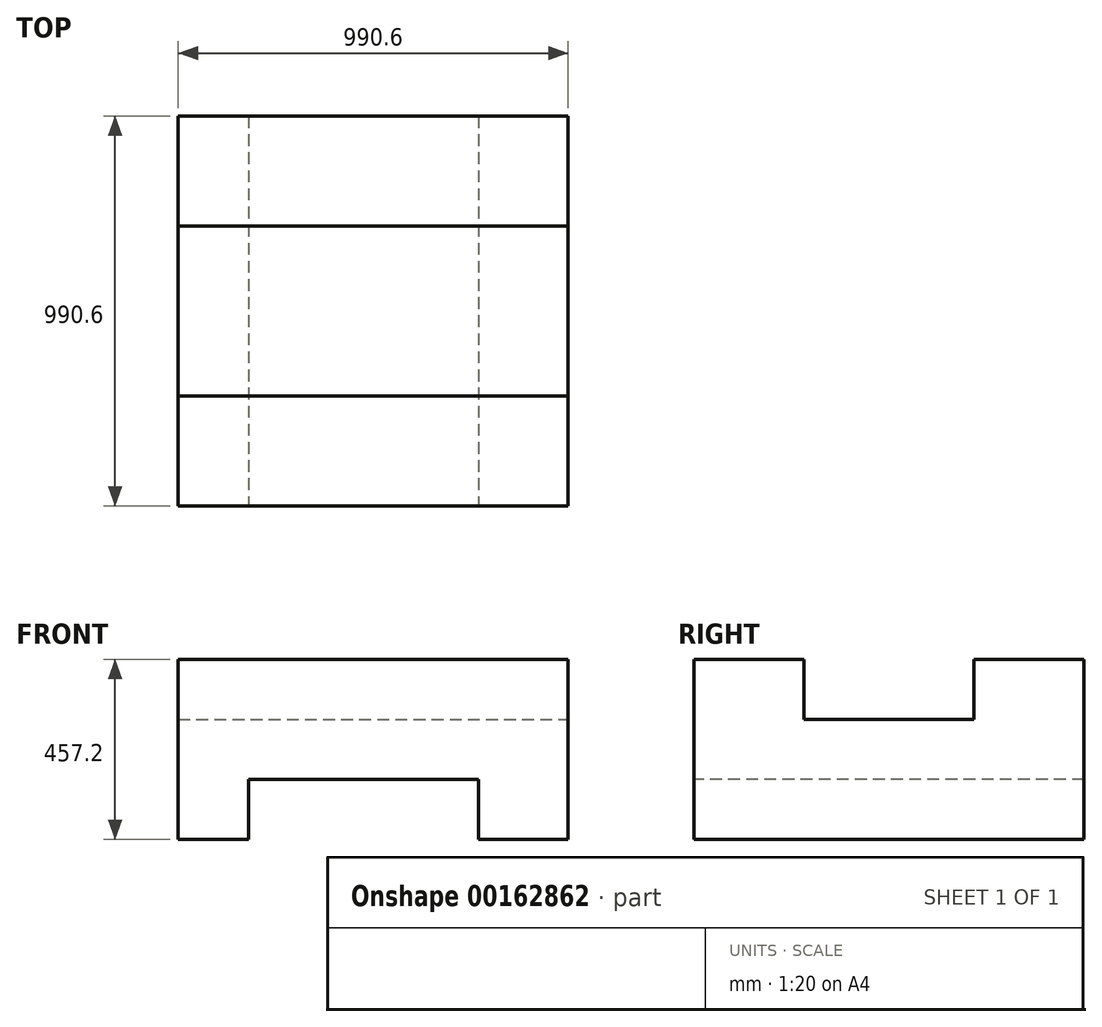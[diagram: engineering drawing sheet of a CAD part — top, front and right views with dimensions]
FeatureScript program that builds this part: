
annotation { "Feature Type Name" : "Feature", "Feature Type Description" : "" }
export const myFeature = defineFeature(function(context is Context, id is Id, definition is map)
    precondition{}
    {
        {
            var Q0;
            Q0=qCreatedBy(makeId("Top.planeOp"),FACE);
            var sketch = newSketch(context, id + "F0", { "sketchPlane" : qUnion([Q0])});
            skLineSegment(sketch, "E0.bottom", {"start": v(495.3, -495.3) * mm, "end": v(-495.3, -495.3) * mm});
            skLineSegment(sketch, "E0.top", {"start": v(495.3, 495.3) * mm, "end": v(-495.3, 495.3) * mm});
            skLineSegment(sketch, "E0.left", {"start": v(495.3, -495.3) * mm, "end": v(495.3, 495.3) * mm});
            skLineSegment(sketch, "E0.right", {"start": v(-495.3, -495.3) * mm, "end": v(-495.3, 495.3) * mm});
            skPoint(sketch, "E0.middle", {"position": v(0, 0) * mm});
            skSolve(sketch);
        }
        {
            var Q0;
            Q0 = qSketchRegion(id + "F0", true);
            extrude(context, id + "F1", {"entities" : qUnion([Q0]), "depth" : 152.4 * mm});
        }
        {
            var Q0;
            Q0=makeQuery(id+"F1.opExtrude","CAP_FACE",FACE,{"disambiguationData":[OSD([sQuery(id+"F0.wireOp",EDGE,"E0.bottom"),sQuery(id+"F0.wireOp",EDGE,"E0.top"),sQuery(id+"F0.wireOp",EDGE,"E0.left"),sQuery(id+"F0.wireOp",EDGE,"E0.right")])],"isStart":false});
            var sketch = newSketch(context, id + "F2", { "sketchPlane" : qUnion([Q0])});
            skLineSegment(sketch, "E1.bottom", {"start": v(-495.3, 495.3) * mm, "end": v(495.3, 495.3) * mm});
            skLineSegment(sketch, "E1.top", {"start": v(-495.3, 215.9) * mm, "end": v(495.3, 215.9) * mm});
            skLineSegment(sketch, "E1.left", {"start": v(-495.3, 495.3) * mm, "end": v(-495.3, 215.9) * mm});
            skLineSegment(sketch, "E1.right", {"start": v(495.3, 495.3) * mm, "end": v(495.3, 215.9) * mm});
            skLineSegment(sketch, "E2.bottom", {"start": v(-495.3, -495.3) * mm, "end": v(495.3, -495.3) * mm});
            skLineSegment(sketch, "E2.top", {"start": v(-495.3, -215.9) * mm, "end": v(495.3, -215.9) * mm});
            skLineSegment(sketch, "E2.left", {"start": v(-495.3, -495.3) * mm, "end": v(-495.3, -215.9) * mm});
            skLineSegment(sketch, "E2.right", {"start": v(495.3, -495.3) * mm, "end": v(495.3, -215.9) * mm});
            skSolve(sketch);
        }
        {
            var Q0;
            Q0 = qSketchRegion(id + "F2", true);
            extrude(context, id + "F3", {"entities" : qUnion([Q0]), "operationType" : NewBodyOperationType.ADD, "depth" : 152.4 * mm});
        }
        {
            var Q0;
            Q0=makeQuery(id+"F1.opExtrude","CAP_FACE",FACE,{"disambiguationData":[OSD([sQuery(id+"F0.wireOp",EDGE,"E0.bottom"),sQuery(id+"F0.wireOp",EDGE,"E0.top"),sQuery(id+"F0.wireOp",EDGE,"E0.left"),sQuery(id+"F0.wireOp",EDGE,"E0.right")])],"isStart":true});
            var sketch = newSketch(context, id + "F4", { "sketchPlane" : qUnion([Q0])});
            skLineSegment(sketch, "E3.bottom", {"start": v(-495.3, -495.3) * mm, "end": v(-316.2, -495.3) * mm});
            skLineSegment(sketch, "E3.top", {"start": v(-495.3, 495.3) * mm, "end": v(-316.2, 495.3) * mm});
            skLineSegment(sketch, "E3.left", {"start": v(-495.3, -495.3) * mm, "end": v(-495.3, 495.3) * mm});
            skLineSegment(sketch, "E3.right", {"start": v(-316.2, -495.3) * mm, "end": v(-316.2, 495.3) * mm});
            skLineSegment(sketch, "E4.bottom", {"start": v(495.3, -495.3) * mm, "end": v(268, -495.3) * mm});
            skLineSegment(sketch, "E4.top", {"start": v(495.3, 495.3) * mm, "end": v(268, 495.3) * mm});
            skLineSegment(sketch, "E4.left", {"start": v(495.3, -495.3) * mm, "end": v(495.3, 495.3) * mm});
            skLineSegment(sketch, "E4.right", {"start": v(268, -495.3) * mm, "end": v(268, 495.3) * mm});
            skSolve(sketch);
        }
        {
            var Q0;
            Q0 = qSketchRegion(id + "F4", true);
            extrude(context, id + "F5", {"entities" : qUnion([Q0]), "operationType" : NewBodyOperationType.ADD, "depth" : 152.4 * mm});
        }
    });
